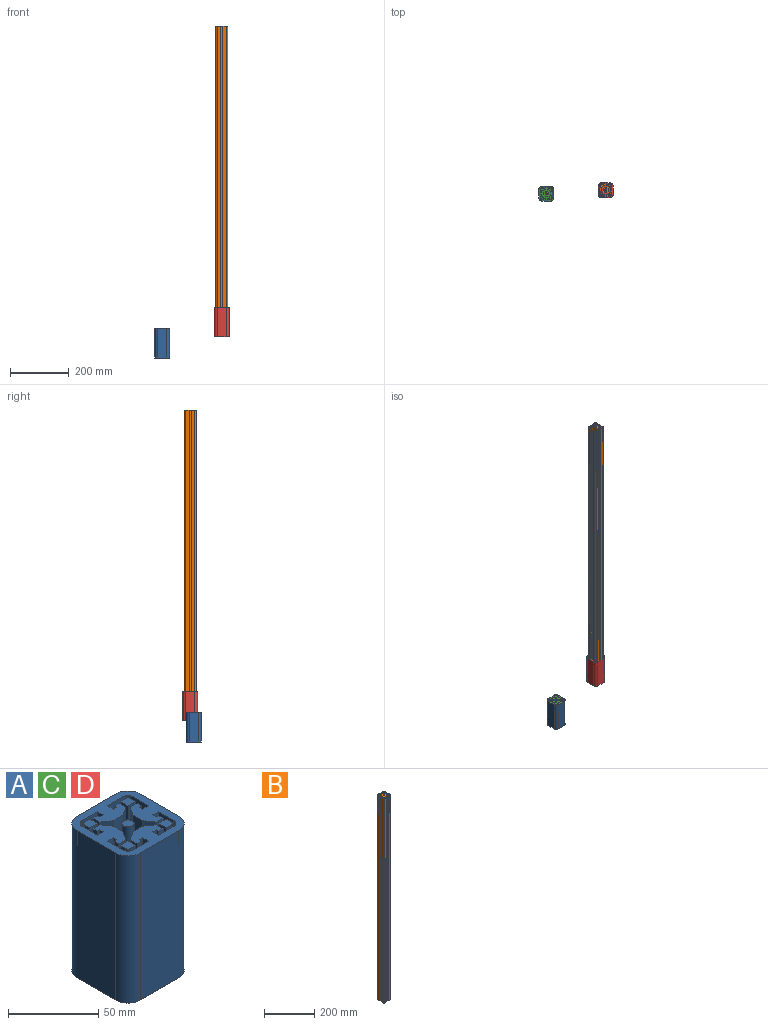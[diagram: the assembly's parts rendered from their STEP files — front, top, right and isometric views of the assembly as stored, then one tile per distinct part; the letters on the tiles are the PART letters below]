
ASSEMBLY  parts=4 mates=1
PART A: 192 faces, bbox 50x50x100 mm
  f0: plane 100x30mm, normal (0,-1,0), area 3000mm2, adj f4,f5,f188,f191
  f1: plane 100x30mm, normal (1,0,0), area 3000mm2, adj f4,f5,f188,f189
  f2: plane 100x30mm, normal (0,1,0), area 3000mm2, adj f4,f5,f189,f190
  f3: plane 100x30mm, normal (-1,0,0), area 3000mm2, adj f4,f5,f190,f191
  f4: plane 50x50mm, normal (0,0,1), area 1551.7mm2, adj f0,f1,f2,f3,f113,f114,f115,f116
  f5: plane 50x50mm, normal (0,0,-1), area 1551.7mm2, adj f0,f1,f2,f3,f22,f23,f24,f25
  f6: plane 40x4mm, normal (0,1,0), area 160mm2, adj f7,f85,f91,f95
  f7: plane 40x6mm, normal (1,0,0), area 240mm2, adj f6,f8,f91,f95
  f8: plane 40x6mm, normal (0,-1,0), area 240mm2, adj f7,f9,f91,f95
  f9: plane 40x4mm, normal (-1,0,0), area 160mm2, adj f8,f85,f91,f95
  f10: plane 40x4mm, normal (0,-1,0), area 160mm2, adj f11,f86,f91,f94
  f11: plane 40x6mm, normal (-1,0,0), area 240mm2, adj f10,f12,f91,f94
  f12: plane 40x6mm, normal (0,1,0), area 240mm2, adj f11,f13,f91,f94
  f13: plane 40x4mm, normal (1,0,0), area 160mm2, adj f12,f86,f91,f94
  f14: plane 40x4mm, normal (-1,0,0), area 160mm2, adj f15,f87,f91,f93
  f15: plane 40x6mm, normal (0,1,0), area 240mm2, adj f14,f16,f91,f93
  f16: plane 40x6mm, normal (1,0,0), area 240mm2, adj f15,f17,f91,f93
  f17: plane 40x4mm, normal (0,-1,0), area 160mm2, adj f16,f87,f91,f93
  f18: plane 40x4mm, normal (1,0,0), area 160mm2, adj f19,f88,f91,f92
  f19: plane 40x6mm, normal (0,-1,0), area 240mm2, adj f18,f20,f91,f92
  f20: plane 40x6mm, normal (-1,0,0), area 240mm2, adj f19,f21,f91,f92
  f21: plane 40x4mm, normal (0,1,0), area 160mm2, adj f20,f88,f91,f92
  f22: plane 40x4.5mm, normal (0,1,0), area 180mm2, adj f5,f23,f89,f91
  f23: plane 40x12mm, normal (-1,0,0), area 480mm2, adj f5,f22,f24,f91
  f24: cylinder r=4mm len=40mm, axis (0,0,-1), area 251.3mm2, adj f5,f23,f25,f91
  f25: plane 40x12mm, normal (0,-1,0), area 480mm2, adj f5,f24,f26,f91
  f26: plane 40x4.5mm, normal (1,0,0), area 180mm2, adj f5,f25,f27,f91
  f27: plane 40x2.72mm, normal (0,1,0), area 108.7mm2, adj f5,f26,f28,f91
  f28: plane 40x1.85mm, normal (-1,0,0), area 74mm2, adj f5,f27,f29,f91
  f29: plane 40x3.5mm, normal (0,1,0), area 140.1mm2, adj f5,f28,f30,f91
  f30: plane 40x5.35mm, normal (1,0,0), area 214mm2, adj f5,f29,f31,f91
  f31: plane 40x6.22mm, normal (0.56,-0.83,0), area 301.4mm2, adj f5,f30,f32,f91
  f32: plane 40x8mm, normal (0,-1,0), area 320mm2, adj f5,f31,f33,f91
  f33: plane 40x6.22mm, normal (-0.56,-0.83,0), area 301.4mm2, adj f5,f32,f34,f91
  f34: plane 40x5.35mm, normal (-1,0,0), area 214mm2, adj f5,f33,f35,f91
  f35: plane 40x3.5mm, normal (0,1,0), area 140.1mm2, adj f5,f34,f36,f91
  f36: plane 40x1.85mm, normal (1,0,0), area 74mm2, adj f5,f35,f37,f91
  f37: plane 40x2.72mm, normal (0,1,0), area 108.7mm2, adj f5,f36,f38,f91
  f38: plane 40x4.5mm, normal (-1,0,0), area 180mm2, adj f5,f37,f39,f91
  f39: plane 40x12mm, normal (0,-1,0), area 480mm2, adj f5,f38,f40,f91
  f40: cylinder r=4mm len=40mm, axis (0,0,-1), area 251.3mm2, adj f5,f39,f41,f91
  f41: plane 40x12mm, normal (1,0,0), area 480mm2, adj f5,f40,f42,f91
  f42: plane 40x4.5mm, normal (0,1,0), area 180mm2, adj f5,f41,f43,f91
  f43: plane 40x2.72mm, normal (-1,0,0), area 108.7mm2, adj f5,f42,f44,f91
  f44: plane 40x1.85mm, normal (0,-1,0), area 74mm2, adj f5,f43,f45,f91
  f45: plane 40x3.5mm, normal (-1,0,0), area 140.1mm2, adj f5,f44,f46,f91
  f46: plane 40x5.35mm, normal (0,1,0), area 214mm2, adj f5,f45,f47,f91
  f47: plane 40x6.22mm, normal (0.83,0.56,0), area 301.4mm2, adj f5,f46,f48,f91
  f48: plane 40x8mm, normal (1,0,0), area 320mm2, adj f5,f47,f49,f91
  f49: plane 40x6.22mm, normal (0.83,-0.56,0), area 301.4mm2, adj f5,f48,f50,f91
  f50: plane 40x5.35mm, normal (0,-1,0), area 214mm2, adj f5,f49,f51,f91
  f51: plane 40x3.5mm, normal (-1,0,0), area 140.1mm2, adj f5,f50,f52,f91
  f52: plane 40x1.85mm, normal (0,1,0), area 74mm2, adj f5,f51,f53,f91
  f53: plane 40x2.72mm, normal (-1,0,0), area 108.7mm2, adj f5,f52,f54,f91
  f54: plane 40x4.5mm, normal (0,-1,0), area 180mm2, adj f5,f53,f55,f91
  f55: plane 40x12mm, normal (1,0,0), area 480mm2, adj f5,f54,f56,f91
  f56: cylinder r=4mm len=40mm, axis (0,0,-1), area 251.3mm2, adj f5,f55,f57,f91
  f57: plane 40x12mm, normal (0,1,0), area 480mm2, adj f5,f56,f58,f91
  f58: plane 40x4.5mm, normal (-1,0,0), area 180mm2, adj f5,f57,f59,f91
  f59: plane 40x2.72mm, normal (0,-1,0), area 108.7mm2, adj f5,f58,f60,f91
  f60: plane 40x1.85mm, normal (1,0,0), area 74mm2, adj f5,f59,f61,f91
  f61: plane 40x3.5mm, normal (0,-1,0), area 140.1mm2, adj f5,f60,f62,f91
  f62: plane 40x5.35mm, normal (-1,0,0), area 214mm2, adj f5,f61,f63,f91
  f63: plane 40x6.22mm, normal (-0.56,0.83,0), area 301.4mm2, adj f5,f62,f64,f91
  f64: plane 40x8mm, normal (0,1,0), area 320mm2, adj f5,f63,f65,f91
  f65: plane 40x6.22mm, normal (0.56,0.83,0), area 301.4mm2, adj f5,f64,f66,f91
  f66: plane 40x5.35mm, normal (1,0,0), area 214mm2, adj f5,f65,f67,f91
  f67: plane 40x3.5mm, normal (0,-1,0), area 140.1mm2, adj f5,f66,f68,f91
  f68: plane 40x1.85mm, normal (-1,0,0), area 74mm2, adj f5,f67,f69,f91
  f69: plane 40x2.72mm, normal (0,-1,0), area 108.7mm2, adj f5,f68,f70,f91
  f70: plane 40x4.5mm, normal (1,0,0), area 180mm2, adj f5,f69,f71,f91
  f71: plane 40x12mm, normal (0,1,0), area 480mm2, adj f5,f70,f72,f91
  f72: cylinder r=4mm len=40mm, axis (0,0,-1), area 251.3mm2, adj f5,f71,f73,f91
  f73: plane 40x12mm, normal (-1,0,0), area 480mm2, adj f5,f72,f74,f91
  f74: plane 40x4.5mm, normal (0,-1,0), area 180mm2, adj f5,f73,f75,f91
  f75: plane 40x2.72mm, normal (1,0,0), area 108.7mm2, adj f5,f74,f76,f91
  f76: plane 40x1.85mm, normal (0,1,0), area 74mm2, adj f5,f75,f77,f91
  f77: plane 40x3.5mm, normal (1,0,0), area 140.1mm2, adj f5,f76,f78,f91
  f78: plane 40x5.35mm, normal (0,-1,0), area 214mm2, adj f5,f77,f79,f91
  f79: plane 40x6.22mm, normal (-0.83,-0.56,0), area 301.4mm2, adj f5,f78,f80,f91
  f80: plane 40x8mm, normal (-1,0,0), area 320mm2, adj f5,f79,f81,f91
  f81: plane 40x6.22mm, normal (-0.83,0.56,0), area 301.4mm2, adj f5,f80,f82,f91
  f82: plane 40x5.35mm, normal (0,1,0), area 214mm2, adj f5,f81,f83,f91
  f83: plane 40x3.5mm, normal (1,0,0), area 140.1mm2, adj f5,f82,f84,f91
  f84: plane 40x1.85mm, normal (0,-1,0), area 74mm2, adj f5,f83,f89,f91
  f85: cylinder r=2mm len=40mm, axis (0,0,-1), area 125.7mm2, adj f6,f9,f91,f95
  f86: cylinder r=2mm len=40mm, axis (0,0,-1), area 125.7mm2, adj f10,f13,f91,f94
  f87: cylinder r=2mm len=40mm, axis (0,0,-1), area 125.7mm2, adj f14,f17,f91,f93
  f88: cylinder r=2mm len=40mm, axis (0,0,-1), area 125.7mm2, adj f18,f21,f91,f92
  f89: plane 40x2.72mm, normal (1,0,0), area 108.7mm2, adj f5,f22,f84,f91
  f90: cylinder r=3.4mm len=40mm, axis (0,0,-1), area 854.5mm2, adj f91,f96
  f91: plane 40x40mm, normal (0,0,-1), area 685.6mm2, adj f6,f7,f8,f9,f10,f11,f12,f13
  f92: plane 6x6mm, normal (0,0,-1), area 35.1mm2, adj f18,f19,f20,f21,f88
  f93: plane 6x6mm, normal (0,0,-1), area 35.1mm2, adj f14,f15,f16,f17,f87
  f94: plane 6x6mm, normal (0,0,-1), area 35.1mm2, adj f10,f11,f12,f13,f86
  f95: plane 6x6mm, normal (0,0,-1), area 35.1mm2, adj f6,f7,f8,f9,f85
  f96: plane 6.8x6.8mm, normal (0,0,-1), area 36.3mm2, adj f90
  f97: plane 40x4mm, normal (0,1,0), area 160mm2, adj f98,f176,f182,f186
  f98: plane 40x6mm, normal (1,0,0), area 240mm2, adj f97,f99,f182,f186
  f99: plane 40x6mm, normal (0,-1,0), area 240mm2, adj f98,f100,f182,f186
  f100: plane 40x4mm, normal (-1,0,0), area 160mm2, adj f99,f176,f182,f186
  f101: plane 40x4mm, normal (0,-1,0), area 160mm2, adj f102,f177,f182,f185
  f102: plane 40x6mm, normal (-1,0,0), area 240mm2, adj f101,f103,f182,f185
  f103: plane 40x6mm, normal (0,1,0), area 240mm2, adj f102,f104,f182,f185
  f104: plane 40x4mm, normal (1,0,0), area 160mm2, adj f103,f177,f182,f185
  f105: plane 40x4mm, normal (-1,0,0), area 160mm2, adj f106,f178,f182,f184
  f106: plane 40x6mm, normal (0,1,0), area 240mm2, adj f105,f107,f182,f184
  f107: plane 40x6mm, normal (1,0,0), area 240mm2, adj f106,f108,f182,f184
  f108: plane 40x4mm, normal (0,-1,0), area 160mm2, adj f107,f178,f182,f184
  f109: plane 40x4mm, normal (1,0,0), area 160mm2, adj f110,f179,f182,f183
  f110: plane 40x6mm, normal (0,-1,0), area 240mm2, adj f109,f111,f182,f183
  f111: plane 40x6mm, normal (-1,0,0), area 240mm2, adj f110,f112,f182,f183
  f112: plane 40x4mm, normal (0,1,0), area 160mm2, adj f111,f179,f182,f183
  f113: plane 40x4.5mm, normal (0,1,0), area 180mm2, adj f4,f114,f180,f182
  f114: plane 40x12mm, normal (-1,0,0), area 480mm2, adj f4,f113,f115,f182
  f115: cylinder r=4mm len=40mm, axis (0,0,1), area 251.3mm2, adj f4,f114,f116,f182
  f116: plane 40x12mm, normal (0,-1,0), area 480mm2, adj f4,f115,f117,f182
  f117: plane 40x4.5mm, normal (1,0,0), area 180mm2, adj f4,f116,f118,f182
  f118: plane 40x2.72mm, normal (0,1,0), area 108.7mm2, adj f4,f117,f119,f182
  f119: plane 40x1.85mm, normal (-1,0,0), area 74mm2, adj f4,f118,f120,f182
  f120: plane 40x3.5mm, normal (0,1,0), area 140.1mm2, adj f4,f119,f121,f182
  f121: plane 40x5.35mm, normal (1,0,0), area 214mm2, adj f4,f120,f122,f182
  f122: plane 40x6.22mm, normal (0.56,-0.83,0), area 301.4mm2, adj f4,f121,f123,f182
  f123: plane 40x8mm, normal (0,-1,0), area 320mm2, adj f4,f122,f124,f182
  f124: plane 40x6.22mm, normal (-0.56,-0.83,0), area 301.4mm2, adj f4,f123,f125,f182
  f125: plane 40x5.35mm, normal (-1,0,0), area 214mm2, adj f4,f124,f126,f182
  f126: plane 40x3.5mm, normal (0,1,0), area 140.1mm2, adj f4,f125,f127,f182
  f127: plane 40x1.85mm, normal (1,0,0), area 74mm2, adj f4,f126,f128,f182
  f128: plane 40x2.72mm, normal (0,1,0), area 108.7mm2, adj f4,f127,f129,f182
  f129: plane 40x4.5mm, normal (-1,0,0), area 180mm2, adj f4,f128,f130,f182
  f130: plane 40x12mm, normal (0,-1,0), area 480mm2, adj f4,f129,f131,f182
  f131: cylinder r=4mm len=40mm, axis (0,0,1), area 251.3mm2, adj f4,f130,f132,f182
  f132: plane 40x12mm, normal (1,0,0), area 480mm2, adj f4,f131,f133,f182
  f133: plane 40x4.5mm, normal (0,1,0), area 180mm2, adj f4,f132,f134,f182
  f134: plane 40x2.72mm, normal (-1,0,0), area 108.7mm2, adj f4,f133,f135,f182
  f135: plane 40x1.85mm, normal (0,-1,0), area 74mm2, adj f4,f134,f136,f182
  f136: plane 40x3.5mm, normal (-1,0,0), area 140.1mm2, adj f4,f135,f137,f182
  f137: plane 40x5.35mm, normal (0,1,0), area 214mm2, adj f4,f136,f138,f182
  f138: plane 40x6.22mm, normal (0.83,0.56,0), area 301.4mm2, adj f4,f137,f139,f182
  f139: plane 40x8mm, normal (1,0,0), area 320mm2, adj f4,f138,f140,f182
  f140: plane 40x6.22mm, normal (0.83,-0.56,0), area 301.4mm2, adj f4,f139,f141,f182
  f141: plane 40x5.35mm, normal (0,-1,0), area 214mm2, adj f4,f140,f142,f182
  f142: plane 40x3.5mm, normal (-1,0,0), area 140.1mm2, adj f4,f141,f143,f182
  f143: plane 40x1.85mm, normal (0,1,0), area 74mm2, adj f4,f142,f144,f182
  f144: plane 40x2.72mm, normal (-1,0,0), area 108.7mm2, adj f4,f143,f145,f182
  f145: plane 40x4.5mm, normal (0,-1,0), area 180mm2, adj f4,f144,f146,f182
  f146: plane 40x12mm, normal (1,0,0), area 480mm2, adj f4,f145,f147,f182
  f147: cylinder r=4mm len=40mm, axis (0,0,1), area 251.3mm2, adj f4,f146,f148,f182
  f148: plane 40x12mm, normal (0,1,0), area 480mm2, adj f4,f147,f149,f182
  f149: plane 40x4.5mm, normal (-1,0,0), area 180mm2, adj f4,f148,f150,f182
  f150: plane 40x2.72mm, normal (0,-1,0), area 108.7mm2, adj f4,f149,f151,f182
  f151: plane 40x1.85mm, normal (1,0,0), area 74mm2, adj f4,f150,f152,f182
  f152: plane 40x3.5mm, normal (0,-1,0), area 140.1mm2, adj f4,f151,f153,f182
  f153: plane 40x5.35mm, normal (-1,0,0), area 214mm2, adj f4,f152,f154,f182
  f154: plane 40x6.22mm, normal (-0.56,0.83,0), area 301.4mm2, adj f4,f153,f155,f182
  f155: plane 40x8mm, normal (0,1,0), area 320mm2, adj f4,f154,f156,f182
  f156: plane 40x6.22mm, normal (0.56,0.83,0), area 301.4mm2, adj f4,f155,f157,f182
  f157: plane 40x5.35mm, normal (1,0,0), area 214mm2, adj f4,f156,f158,f182
  f158: plane 40x3.5mm, normal (0,-1,0), area 140.1mm2, adj f4,f157,f159,f182
  f159: plane 40x1.85mm, normal (-1,0,0), area 74mm2, adj f4,f158,f160,f182
  f160: plane 40x2.72mm, normal (0,-1,0), area 108.7mm2, adj f4,f159,f161,f182
  f161: plane 40x4.5mm, normal (1,0,0), area 180mm2, adj f4,f160,f162,f182
  f162: plane 40x12mm, normal (0,1,0), area 480mm2, adj f4,f161,f163,f182
  f163: cylinder r=4mm len=40mm, axis (0,0,1), area 251.3mm2, adj f4,f162,f164,f182
  f164: plane 40x12mm, normal (-1,0,0), area 480mm2, adj f4,f163,f165,f182
  f165: plane 40x4.5mm, normal (0,-1,0), area 180mm2, adj f4,f164,f166,f182
  f166: plane 40x2.72mm, normal (1,0,0), area 108.7mm2, adj f4,f165,f167,f182
  f167: plane 40x1.85mm, normal (0,1,0), area 74mm2, adj f4,f166,f168,f182
  f168: plane 40x3.5mm, normal (1,0,0), area 140.1mm2, adj f4,f167,f169,f182
  f169: plane 40x5.35mm, normal (0,-1,0), area 214mm2, adj f4,f168,f170,f182
  f170: plane 40x6.22mm, normal (-0.83,-0.56,0), area 301.4mm2, adj f4,f169,f171,f182
  f171: plane 40x8mm, normal (-1,0,0), area 320mm2, adj f4,f170,f172,f182
  f172: plane 40x6.22mm, normal (-0.83,0.56,0), area 301.4mm2, adj f4,f171,f173,f182
  f173: plane 40x5.35mm, normal (0,1,0), area 214mm2, adj f4,f172,f174,f182
  f174: plane 40x3.5mm, normal (1,0,0), area 140.1mm2, adj f4,f173,f175,f182
  f175: plane 40x1.85mm, normal (0,-1,0), area 74mm2, adj f4,f174,f180,f182
  f176: cylinder r=2mm len=40mm, axis (0,0,1), area 125.7mm2, adj f97,f100,f182,f186
  f177: cylinder r=2mm len=40mm, axis (0,0,1), area 125.7mm2, adj f101,f104,f182,f185
  f178: cylinder r=2mm len=40mm, axis (0,0,1), area 125.7mm2, adj f105,f108,f182,f184
  f179: cylinder r=2mm len=40mm, axis (0,0,1), area 125.7mm2, adj f109,f112,f182,f183
  f180: plane 40x2.72mm, normal (1,0,0), area 108.7mm2, adj f4,f113,f175,f182
  f181: cylinder r=3.4mm len=40mm, axis (0,0,1), area 854.5mm2, adj f182,f187
  f182: plane 40x40mm, normal (0,0,1), area 685.6mm2, adj f97,f98,f99,f100,f101,f102,f103,f104
  f183: plane 6x6mm, normal (0,0,1), area 35.1mm2, adj f109,f110,f111,f112,f179
  f184: plane 6x6mm, normal (0,0,1), area 35.1mm2, adj f105,f106,f107,f108,f178
  f185: plane 6x6mm, normal (0,0,1), area 35.1mm2, adj f101,f102,f103,f104,f177
  f186: plane 6x6mm, normal (0,0,1), area 35.1mm2, adj f97,f98,f99,f100,f176
  f187: plane 6.8x6.8mm, normal (0,0,1), area 36.3mm2, adj f181
  f188: cylinder r=10mm len=100mm, axis (0,0,1), area 1570.8mm2, adj f0,f1,f4,f5
  f189: cylinder r=10mm len=100mm, axis (0,0,-1), area 1570.8mm2, adj f1,f2,f4,f5
  f190: cylinder r=10mm len=100mm, axis (0,0,1), area 1570.8mm2, adj f2,f3,f4,f5
  f191: cylinder r=10mm len=100mm, axis (0,0,-1), area 1570.8mm2, adj f0,f3,f4,f5
PART B: 87 faces, bbox 40x40x1000 mm
  f0: plane 1000x12mm, normal (0,-1,0), area 12000mm2, adj f3,f12,f47,f86
  f1: plane 1000x12mm, normal (1,0,0), area 12000mm2, adj f3,f6,f75,f86
  f2: plane 1000x12mm, normal (0,1,0), area 12000mm2, adj f3,f8,f60,f86
  f3: plane 40x40mm, normal (0,0,-1), area 685.6mm2, adj f0,f1,f2,f4,f5,f6,f7,f8
  f4: plane 1000x12mm, normal (-1,0,0), area 12000mm2, adj f3,f10,f37,f86
  f5: plane 1000x12mm, normal (0,-1,0), area 12000mm2, adj f3,f6,f59,f86
  f6: cylinder r=4mm len=1000mm, axis (0,0,-1), area 6283.2mm2, adj f1,f3,f5,f86
  f7: plane 1000x12mm, normal (1,0,0), area 12000mm2, adj f3,f8,f74,f86
  f8: cylinder r=4mm len=1000mm, axis (0,0,-1), area 6283.2mm2, adj f2,f3,f7,f86
  f9: plane 1000x12mm, normal (0,1,0), area 12000mm2, adj f3,f10,f72,f86
  f10: cylinder r=4mm len=1000mm, axis (0,0,-1), area 6283.2mm2, adj f3,f4,f9,f86
  f11: plane 1000x12mm, normal (-1,0,0), area 12000mm2, adj f3,f12,f36,f86
  f12: cylinder r=4mm len=1000mm, axis (0,0,-1), area 6283.2mm2, adj f0,f3,f11,f86
  f13: cylinder r=3.4mm len=1000mm, axis (0,0,-1), area 21362.8mm2, adj f3,f86
  f14: plane 1000x4mm, normal (0,-1,0), area 4000mm2, adj f3,f15,f18,f86
  f15: plane 1000x6mm, normal (-1,0,0), area 6000mm2, adj f3,f14,f16,f86
  f16: plane 1000x6mm, normal (0,1,0), area 6000mm2, adj f3,f15,f17,f86
  f17: plane 1000x4mm, normal (1,0,0), area 4000mm2, adj f3,f16,f18,f86
  f18: cylinder r=2mm len=1000mm, axis (0,0,1), area 3141.6mm2, adj f3,f14,f17,f86
  f19: plane 1000x4mm, normal (0,1,0), area 4000mm2, adj f3,f20,f23,f86
  f20: plane 1000x6mm, normal (1,0,0), area 6000mm2, adj f3,f19,f21,f86
  f21: plane 1000x6mm, normal (0,-1,0), area 6000mm2, adj f3,f20,f22,f86
  f22: plane 1000x4mm, normal (-1,0,0), area 4000mm2, adj f3,f21,f23,f86
  f23: cylinder r=2mm len=1000mm, axis (0,0,1), area 3141.6mm2, adj f3,f19,f22,f86
  f24: plane 1000x4mm, normal (1,0,0), area 4000mm2, adj f3,f25,f28,f86
  f25: plane 1000x6mm, normal (0,-1,0), area 6000mm2, adj f3,f24,f26,f86
  f26: plane 1000x6mm, normal (-1,0,0), area 6000mm2, adj f3,f25,f27,f86
  f27: plane 1000x4mm, normal (0,1,0), area 4000mm2, adj f3,f26,f28,f86
  f28: cylinder r=2mm len=1000mm, axis (0,0,1), area 3141.6mm2, adj f3,f24,f27,f86
  f29: plane 1000x4mm, normal (-1,0,0), area 4000mm2, adj f3,f30,f33,f86
  f30: plane 1000x6mm, normal (0,1,0), area 6000mm2, adj f3,f29,f31,f86
  f31: plane 1000x6mm, normal (1,0,0), area 6000mm2, adj f3,f30,f32,f86
  f32: plane 1000x4mm, normal (0,-1,0), area 4000mm2, adj f3,f31,f33,f86
  f33: cylinder r=2mm len=1000mm, axis (0,0,1), area 3141.6mm2, adj f3,f29,f32,f86
  f34: plane 1000x1.85mm, normal (0,-1,0), area 1850mm2, adj f3,f35,f46,f86
  f35: plane 1000x2.72mm, normal (1,0,0), area 2717.9mm2, adj f3,f34,f36,f86
  f36: plane 1000x4.5mm, normal (0,1,0), area 4500mm2, adj f3,f11,f35,f86
  f37: plane 1000x4.5mm, normal (0,-1,0), area 4500mm2, adj f3,f4,f38,f86
  f38: plane 1000x2.72mm, normal (1,0,0), area 2717.9mm2, adj f3,f37,f39,f86
  f39: plane 1000x1.85mm, normal (0,1,0), area 1850mm2, adj f3,f38,f40,f86
  f40: plane 1000x3.5mm, normal (1,0,0), area 3503mm2, adj f3,f39,f41,f86
  f41: plane 1000x5.35mm, normal (0,-1,0), area 5350mm2, adj f3,f40,f42,f86
  f42: plane 1000x6.22mm, normal (-0.83,-0.56,0), area 7534.1mm2, adj f3,f41,f43,f86
  f43: plane 1000x8mm, normal (-1,0,0), area 8000mm2, adj f3,f42,f44,f86
  f44: plane 1000x6.22mm, normal (-0.83,0.56,0), area 7534.1mm2, adj f3,f43,f45,f86
  f45: plane 1000x5.35mm, normal (0,1,0), area 5350mm2, adj f3,f44,f46,f86
  f46: plane 1000x3.5mm, normal (1,0,0), area 3503mm2, adj f3,f34,f45,f86
  f47: plane 1000x4.5mm, normal (1,0,0), area 4500mm2, adj f0,f3,f48,f86
  f48: plane 1000x2.72mm, normal (0,1,0), area 2717.9mm2, adj f3,f47,f49,f86
  f49: plane 1000x1.85mm, normal (-1,0,0), area 1850mm2, adj f3,f48,f50,f86
  f50: plane 1000x3.5mm, normal (0,1,0), area 3503mm2, adj f3,f49,f51,f86
  f51: plane 1000x5.35mm, normal (1,0,0), area 5350mm2, adj f3,f50,f52,f86
  f52: plane 1000x6.22mm, normal (0.56,-0.83,0), area 7534.1mm2, adj f3,f51,f53,f86
  f53: plane 1000x8mm, normal (0,-1,0), area 8000mm2, adj f3,f52,f54,f86
  f54: plane 1000x6.22mm, normal (-0.56,-0.83,0), area 7534.1mm2, adj f3,f53,f55,f86
  f55: plane 1000x5.35mm, normal (-1,0,0), area 5350mm2, adj f3,f54,f56,f86
  f56: plane 1000x3.5mm, normal (0,1,0), area 3503mm2, adj f3,f55,f57,f86
  f57: plane 1000x1.85mm, normal (1,0,0), area 1850mm2, adj f3,f56,f58,f86
  f58: plane 1000x2.72mm, normal (0,1,0), area 2717.9mm2, adj f3,f57,f59,f86
  f59: plane 1000x4.5mm, normal (-1,0,0), area 4500mm2, adj f3,f5,f58,f86
  f60: plane 1000x4.5mm, normal (-1,0,0), area 4500mm2, adj f2,f3,f61,f86
  f61: plane 1000x2.72mm, normal (0,-1,0), area 2717.9mm2, adj f3,f60,f62,f86
  f62: plane 1000x1.85mm, normal (1,0,0), area 1850mm2, adj f3,f61,f63,f86
  f63: plane 1000x3.5mm, normal (0,-1,0), area 3503mm2, adj f3,f62,f64,f86
  f64: plane 1000x5.35mm, normal (-1,0,0), area 5350mm2, adj f3,f63,f65,f86
  f65: plane 1000x6.22mm, normal (-0.56,0.83,0), area 7534.1mm2, adj f3,f64,f66,f86
  f66: plane 1000x8mm, normal (0,1,0), area 8000mm2, adj f3,f65,f67,f86
  f67: plane 1000x6.22mm, normal (0.56,0.83,0), area 7534.1mm2, adj f3,f66,f68,f86
  f68: plane 1000x5.35mm, normal (1,0,0), area 5350mm2, adj f3,f67,f69,f86
  f69: plane 1000x3.5mm, normal (0,-1,0), area 3503mm2, adj f3,f68,f70,f86
  f70: plane 1000x1.85mm, normal (-1,0,0), area 1850mm2, adj f3,f69,f71,f86
  f71: plane 1000x2.72mm, normal (0,-1,0), area 2717.9mm2, adj f3,f70,f72,f86
  f72: plane 1000x4.5mm, normal (1,0,0), area 4500mm2, adj f3,f9,f71,f86
  f73: plane 1000x2.72mm, normal (-1,0,0), area 2717.9mm2, adj f3,f74,f85,f86
  f74: plane 1000x4.5mm, normal (0,-1,0), area 4500mm2, adj f3,f7,f73,f86
  f75: plane 1000x4.5mm, normal (0,1,0), area 4500mm2, adj f1,f3,f76,f86
  f76: plane 1000x2.72mm, normal (-1,0,0), area 2717.9mm2, adj f3,f75,f77,f86
  f77: plane 1000x1.85mm, normal (0,-1,0), area 1850mm2, adj f3,f76,f78,f86
  f78: plane 1000x3.5mm, normal (-1,0,0), area 3503mm2, adj f3,f77,f79,f86
  f79: plane 1000x5.35mm, normal (0,1,0), area 5350mm2, adj f3,f78,f80,f86
  f80: plane 1000x6.22mm, normal (0.83,0.56,0), area 7534.1mm2, adj f3,f79,f81,f86
  f81: plane 1000x8mm, normal (1,0,0), area 8000mm2, adj f3,f80,f82,f86
  f82: plane 1000x6.22mm, normal (0.83,-0.56,0), area 7534.1mm2, adj f3,f81,f83,f86
  f83: plane 1000x5.35mm, normal (0,-1,0), area 5350mm2, adj f3,f82,f84,f86
  f84: plane 1000x3.5mm, normal (-1,0,0), area 3503mm2, adj f3,f83,f85,f86
  f85: plane 1000x1.85mm, normal (0,1,0), area 1850mm2, adj f3,f73,f84,f86
  f86: plane 40x40mm, normal (0,0,1), area 685.6mm2, adj f0,f1,f2,f4,f5,f6,f7,f8
PART C: same geometry as A
PART D: same geometry as A
PLACE A t=(92.36,-103.79,-122.21)mm
PLACE B rot(axis=(0.71,0.71,0),180deg) t=(315.37,-111.88,1009.7)mm
PLACE C t=(92.36,-103.79,-122.21)mm
PLACE D t=(295.37,-91.88,-50.3)mm
MATE fastened B.f86 <-> D.f182  axis (0,0,-1) through (283.37,-103.88,9.7)mm
